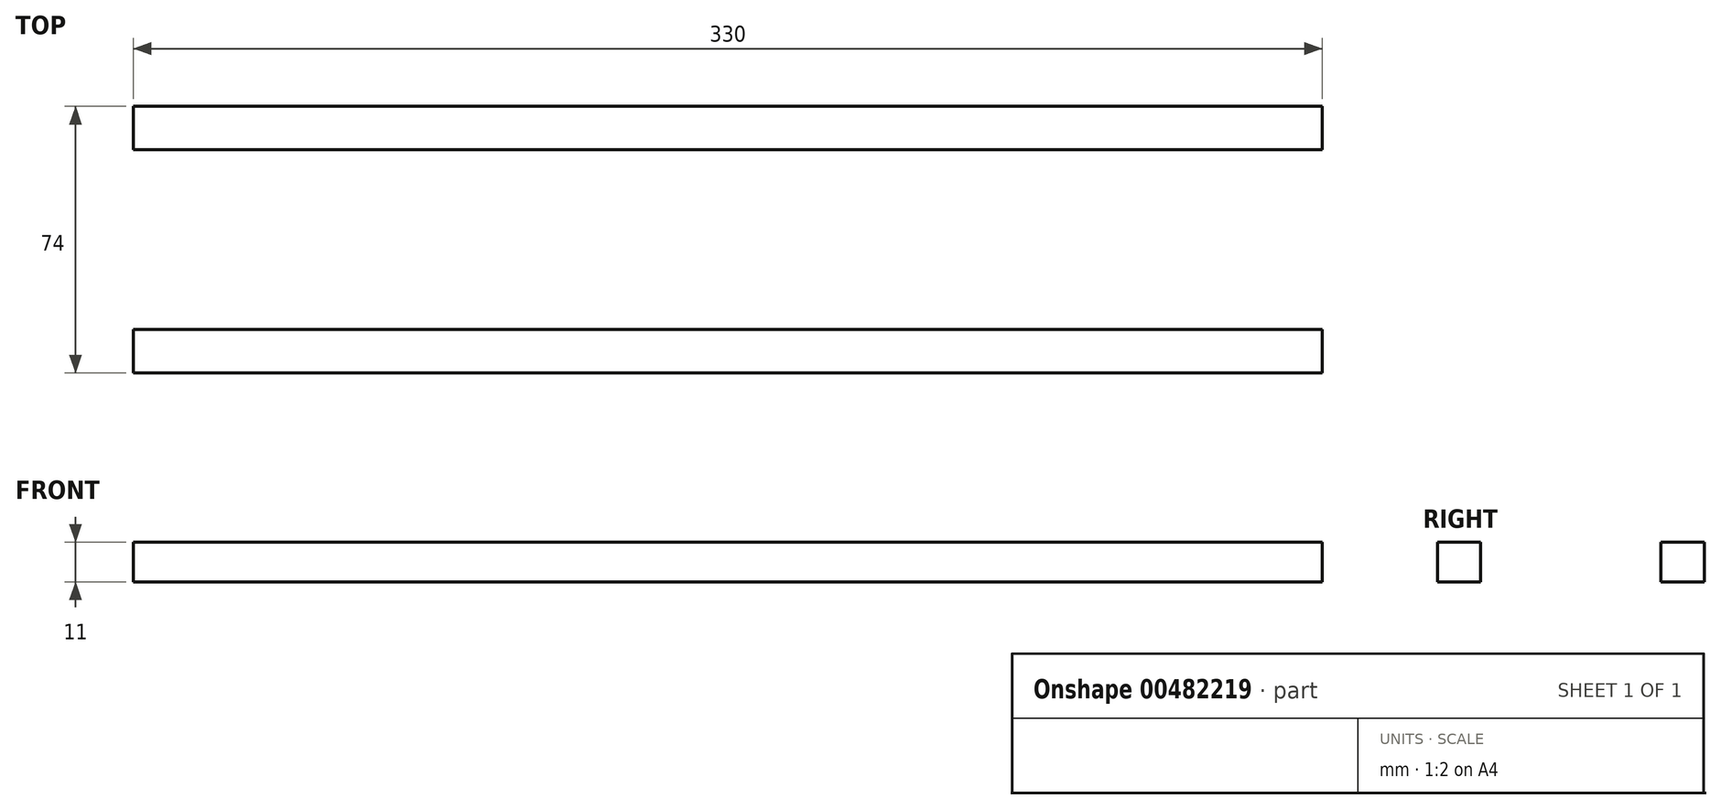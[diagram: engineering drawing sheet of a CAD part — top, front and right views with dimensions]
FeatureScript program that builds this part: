
annotation { "Feature Type Name" : "Feature", "Feature Type Description" : "" }
export const myFeature = defineFeature(function(context is Context, id is Id, definition is map)
    precondition{}
    {
        {
            var Q0;
            Q0=qCreatedBy(makeId("Top.planeOp"),FACE);
            var sketch = newSketch(context, id + "F0", { "sketchPlane" : qUnion([Q0])});
            skLineSegment(sketch, "E0.bottom", {"start": v(0, 0) * mm, "end": v(500, 0) * mm});
            skLineSegment(sketch, "E0.top", {"start": v(0, 350) * mm, "end": v(500, 350) * mm});
            skLineSegment(sketch, "E0.left", {"start": v(0, 0) * mm, "end": v(0, 350) * mm});
            skLineSegment(sketch, "E0.right", {"start": v(500, 0) * mm, "end": v(500, 350) * mm});
            skLineSegment(sketch, "E1.bottom", {"start": v(155, 63) * mm, "end": v(485, 63) * mm});
            skLineSegment(sketch, "E1.top", {"start": v(155, 75) * mm, "end": v(485, 75) * mm});
            skLineSegment(sketch, "E1.left", {"start": v(155, 63) * mm, "end": v(155, 75) * mm});
            skLineSegment(sketch, "E1.right", {"start": v(485, 63) * mm, "end": v(485, 75) * mm});
            skLineSegment(sketch, "E2.bottom", {"start": v(155, 125) * mm, "end": v(485, 125) * mm});
            skLineSegment(sketch, "E2.top", {"start": v(155, 137) * mm, "end": v(485, 137) * mm});
            skLineSegment(sketch, "E2.left", {"start": v(155, 125) * mm, "end": v(155, 137) * mm});
            skLineSegment(sketch, "E2.right", {"start": v(485, 125) * mm, "end": v(485, 137) * mm});
            skLineSegment(sketch, "E3", {"start": v(115, 135) * mm, "end": v(115, 135) * mm});
            skCircle(sketch, "E4", {"center": v(107, 135) * mm, "radius": 3 * mm});
            skCircle(sketch, "E5.MirrorC", {"center": v(123, 135) * mm, "radius": 3 * mm});
            skCircle(sketch, "E6", {"center": v(107, 65) * mm, "radius": 3 * mm});
            skCircle(sketch, "E7.MirrorC", {"center": v(123, 65) * mm, "radius": 3 * mm});
            skPoint(sketch, "E8", {"position": v(320, 42.5) * mm});
            skPoint(sketch, "E9", {"position": v(245, 42.5) * mm});
            skPoint(sketch, "E10", {"position": v(395, 42.5) * mm});
            skCircle(sketch, "E11", {"center": v(170, 42.5) * mm, "radius": 3 * mm});
            skCircle(sketch, "E12", {"center": v(245, 42.5) * mm, "radius": 3 * mm});
            skCircle(sketch, "E13", {"center": v(320, 42.5) * mm, "radius": 3 * mm});
            skCircle(sketch, "E14", {"center": v(395, 42.5) * mm, "radius": 3 * mm});
            skCircle(sketch, "E15", {"center": v(470, 42.5) * mm, "radius": 3 * mm});
            skCircle(sketch, "E16.MirrorC", {"center": v(395, 157.5) * mm, "radius": 3 * mm});
            skCircle(sketch, "E17.MirrorC", {"center": v(245, 157.5) * mm, "radius": 3 * mm});
            skCircle(sketch, "E18.MirrorC", {"center": v(320, 157.5) * mm, "radius": 3 * mm});
            skCircle(sketch, "E19.MirrorC", {"center": v(170, 157.5) * mm, "radius": 3 * mm});
            skCircle(sketch, "E20.MirrorC", {"center": v(470, 157.5) * mm, "radius": 3 * mm});
            skCircle(sketch, "E21", {"center": v(478.61, 256.5) * mm, "radius": 2.5 * mm});
            skCircle(sketch, "E22", {"center": v(478.54, 298.5) * mm, "radius": 2.5 * mm});
            skCircle(sketch, "E23.MirrorC", {"center": v(123.46, 298.5) * mm, "radius": 2.5 * mm});
            skCircle(sketch, "E24.MirrorC", {"center": v(123.39, 256.5) * mm, "radius": 2.5 * mm});
            skLineSegment(sketch, "E25.bottom", {"start": v(91.34, 620.44) * mm, "end": v(104.34, 620.44) * mm});
            skLineSegment(sketch, "E25.top", {"start": v(91.34, 579.44) * mm, "end": v(104.34, 579.44) * mm});
            skLineSegment(sketch, "E25.left", {"start": v(91.34, 620.44) * mm, "end": v(91.34, 579.44) * mm});
            skLineSegment(sketch, "E25.right", {"start": v(104.34, 620.44) * mm, "end": v(104.34, 579.44) * mm});
            skCircle(sketch, "E26", {"center": v(97.96, 583.94) * mm, "radius": 2.5 * mm});
            skCircle(sketch, "E27", {"center": v(97.88, 615.94) * mm, "radius": 2.5 * mm});
            skSolve(sketch);
        }
        {
            var Q0;
            Q0=makeQuery(id+"F0.imprint","IMPRINT",FACE,{"disambiguationData":[TD([[makeQuery(id+"F0.imprint","IMPRINT",EDGE,{"derivedFrom":sQuery(id+"F0.wireOp",EDGE,"E0.bottom")}),1.0]])]});
            var Q1;
            Q1=makeQuery(id+"F0.imprint","IMPRINT",FACE,{"disambiguationData":[TD([[makeQuery(id+"F0.imprint","IMPRINT",EDGE,{"derivedFrom":sQuery(id+"F0.wireOp",EDGE,"uNRts3Xr-A0tI-6eeH-C82y-h4EAb9lMHTzn.bottom")}),-1.0]])]});
            var Q2;
            Q2=makeQuery(id+"F0.imprint","IMPRINT",FACE,{"disambiguationData":[TD([[makeQuery(id+"F0.imprint","IMPRINT",EDGE,{"derivedFrom":sQuery(id+"F0.wireOp",EDGE,"E2.bottom")}),1.0]])]});
            var Q3;
            Q3=makeQuery(id+"F0.imprint","IMPRINT",FACE,{"disambiguationData":[TD([[makeQuery(id+"F0.imprint","IMPRINT",EDGE,{"derivedFrom":sQuery(id+"F0.wireOp",EDGE,"4c47dcb6-4724-46bd-bd65-4ab124e978fb0.MirrorCS")}),1.0]])]});
            var Q4;
            Q4=makeQuery(id+"F0.imprint","IMPRINT",FACE,{"disambiguationData":[TD([[makeQuery(id+"F0.imprint","IMPRINT",EDGE,{"derivedFrom":sQuery(id+"F0.wireOp",EDGE,"a6b73269-a802-4449-93f2-79380c040cbc.bottom")}),-1.0]])]});
            var Q5;
            Q5=makeQuery(id+"F0.imprint","IMPRINT",FACE,{"disambiguationData":[TD([[makeQuery(id+"F0.imprint","IMPRINT",EDGE,{"derivedFrom":sQuery(id+"F0.wireOp",EDGE,"yu3ANbIo-FdIO-HU7t-2UAq-bTAXw5hcEbcA.bottom")}),-1.0]])]});
            var Q6;
            Q6=makeQuery(id+"F0.imprint","IMPRINT",FACE,{"disambiguationData":[TD([[makeQuery(id+"F0.imprint","IMPRINT",EDGE,{"derivedFrom":sQuery(id+"F0.wireOp",EDGE,"E17.MirrorC")}),-1.0]])]});
            var Q7;
            Q7=makeQuery(id+"F0.imprint","IMPRINT",FACE,{"disambiguationData":[TD([[makeQuery(id+"F0.imprint","IMPRINT",EDGE,{"derivedFrom":sQuery(id+"F0.wireOp",EDGE,"E16.MirrorC")}),-1.0]])]});
            var Q8;
            Q8=makeQuery(id+"F0.imprint","IMPRINT",FACE,{"disambiguationData":[TD([[makeQuery(id+"F0.imprint","IMPRINT",EDGE,{"derivedFrom":sQuery(id+"F0.wireOp",EDGE,"E15")}),1.0]])]});
            var Q9;
            Q9=makeQuery(id+"F0.imprint","IMPRINT",FACE,{"disambiguationData":[TD([[makeQuery(id+"F0.imprint","IMPRINT",EDGE,{"derivedFrom":sQuery(id+"F0.wireOp",EDGE,"E14")}),1.0]])]});
            var Q10;
            Q10=makeQuery(id+"F0.imprint","IMPRINT",FACE,{"disambiguationData":[TD([[makeQuery(id+"F0.imprint","IMPRINT",EDGE,{"derivedFrom":sQuery(id+"F0.wireOp",EDGE,"E13")}),1.0]])]});
            var Q11;
            Q11=makeQuery(id+"F0.imprint","IMPRINT",FACE,{"disambiguationData":[TD([[makeQuery(id+"F0.imprint","IMPRINT",EDGE,{"derivedFrom":sQuery(id+"F0.wireOp",EDGE,"E11")}),1.0]])]});
            var Q12;
            Q12=makeQuery(id+"F0.imprint","IMPRINT",FACE,{"disambiguationData":[TD([[makeQuery(id+"F0.imprint","IMPRINT",EDGE,{"derivedFrom":sQuery(id+"F0.wireOp",EDGE,"E12")}),1.0]])]});
            var Q13;
            Q13=makeQuery(id+"F0.imprint","IMPRINT",FACE,{"disambiguationData":[TD([[makeQuery(id+"F0.imprint","IMPRINT",EDGE,{"derivedFrom":sQuery(id+"F0.wireOp",EDGE,"E7.MirrorC")}),-1.0]])]});
            var Q14;
            Q14=makeQuery(id+"F0.imprint","IMPRINT",FACE,{"disambiguationData":[TD([[makeQuery(id+"F0.imprint","IMPRINT",EDGE,{"derivedFrom":sQuery(id+"F0.wireOp",EDGE,"E6")}),1.0]])]});
            var Q15;
            Q15=makeQuery(id+"F0.imprint","IMPRINT",FACE,{"disambiguationData":[TD([[makeQuery(id+"F0.imprint","IMPRINT",EDGE,{"derivedFrom":sQuery(id+"F0.wireOp",EDGE,"E5.MirrorC")}),-1.0]])]});
            var Q16;
            Q16=makeQuery(id+"F0.imprint","IMPRINT",FACE,{"disambiguationData":[TD([[makeQuery(id+"F0.imprint","IMPRINT",EDGE,{"derivedFrom":sQuery(id+"F0.wireOp",EDGE,"E19.MirrorC")}),-1.0]])]});
            var Q17;
            Q17=makeQuery(id+"F0.imprint","IMPRINT",FACE,{"disambiguationData":[TD([[makeQuery(id+"F0.imprint","IMPRINT",EDGE,{"derivedFrom":sQuery(id+"F0.wireOp",EDGE,"E18.MirrorC")}),-1.0]])]});
            var Q18;
            Q18=makeQuery(id+"F0.imprint","IMPRINT",FACE,{"disambiguationData":[TD([[makeQuery(id+"F0.imprint","IMPRINT",EDGE,{"derivedFrom":sQuery(id+"F0.wireOp",EDGE,"E20.MirrorC")}),-1.0]])]});
            var Q19;
            Q19=makeQuery(id+"F0.imprint","IMPRINT",FACE,{"disambiguationData":[TD([[makeQuery(id+"F0.imprint","IMPRINT",EDGE,{"derivedFrom":sQuery(id+"F0.wireOp",EDGE,"E4")}),1.0]])]});
            var Q20;
            Q20=makeQuery(id+"F0.imprint","IMPRINT",FACE,{"disambiguationData":[TD([[makeQuery(id+"F0.imprint","IMPRINT",EDGE,{"derivedFrom":sQuery(id+"F0.wireOp",EDGE,"E22")}),1.0]])]});
            var Q21;
            Q21=makeQuery(id+"F0.imprint","IMPRINT",FACE,{"disambiguationData":[TD([[makeQuery(id+"F0.imprint","IMPRINT",EDGE,{"derivedFrom":sQuery(id+"F0.wireOp",EDGE,"309a9aaa-b51d-4d3a-aa64-c8353506e3b9")}),1.0]])]});
            var Q22;
            Q22=makeQuery(id+"F0.imprint","IMPRINT",FACE,{"disambiguationData":[TD([[makeQuery(id+"F0.imprint","IMPRINT",EDGE,{"derivedFrom":sQuery(id+"F0.wireOp",EDGE,"f062ca2c-7df7-48ee-b907-5a2952540d44")}),1.0]])]});
            var Q23;
            Q23=makeQuery(id+"F0.imprint","IMPRINT",FACE,{"disambiguationData":[TD([[makeQuery(id+"F0.imprint","IMPRINT",EDGE,{"derivedFrom":sQuery(id+"F0.wireOp",EDGE,"E21")}),1.0]])]});
            var Q24;
            Q24=makeQuery(id+"F0.imprint","IMPRINT",FACE,{"disambiguationData":[TD([[makeQuery(id+"F0.imprint","IMPRINT",EDGE,{"derivedFrom":sQuery(id+"F0.wireOp",EDGE,"E23.MirrorC")}),-1.0]])]});
            var Q25;
            Q25=makeQuery(id+"F0.imprint","IMPRINT",FACE,{"disambiguationData":[TD([[makeQuery(id+"F0.imprint","IMPRINT",EDGE,{"derivedFrom":sQuery(id+"F0.wireOp",EDGE,"E24.MirrorC")}),-1.0]])]});
            var Q26;
            Q26=makeQuery(id+"F0.imprint","IMPRINT",FACE,{"disambiguationData":[TD([[makeQuery(id+"F0.imprint","IMPRINT",EDGE,{"derivedFrom":sQuery(id+"F0.wireOp",EDGE,"E1.bottom")}),1.0]])]});
            extrude(context, id + "F1", {"entities" : qUnion([Q0, Q1, Q2, Q3, Q4, Q5, Q6, Q7, Q8, Q9, Q10, Q11, Q12, Q13, Q14, Q15, Q16, Q17, Q18, Q19, Q20, Q21, Q22, Q23, Q24, Q25, Q26]), "oppositeDirection" : true, "depth" : 20 * mm});
        }
        {
            var Q0;
            Q0=makeQuery(id+"F0.imprint","IMPRINT",FACE,{"disambiguationData":[TD([[makeQuery(id+"F0.imprint","IMPRINT",EDGE,{"derivedFrom":sQuery(id+"F0.wireOp",EDGE,"E2.bottom")}),1.0]])]});
            var Q1;
            Q1=makeQuery(id+"F0.imprint","IMPRINT",FACE,{"disambiguationData":[TD([[makeQuery(id+"F0.imprint","IMPRINT",EDGE,{"derivedFrom":sQuery(id+"F0.wireOp",EDGE,"E1.bottom")}),1.0]])]});
            extrude(context, id + "F2", {"entities" : qUnion([Q0, Q1]), "operationType" : NewBodyOperationType.REMOVE, "oppositeDirection" : true, "depth" : 9 * mm});
        }
        {
            var Q0;
            Q0=makeQuery(id+"F0.imprint","IMPRINT",FACE,{"disambiguationData":[TD([[makeQuery(id+"F0.imprint","IMPRINT",EDGE,{"derivedFrom":sQuery(id+"F0.wireOp",EDGE,"E11")}),1.0]])]});
            var Q1;
            Q1=makeQuery(id+"F0.imprint","IMPRINT",FACE,{"disambiguationData":[TD([[makeQuery(id+"F0.imprint","IMPRINT",EDGE,{"derivedFrom":sQuery(id+"F0.wireOp",EDGE,"E12")}),1.0]])]});
            var Q2;
            Q2=makeQuery(id+"F0.imprint","IMPRINT",FACE,{"disambiguationData":[TD([[makeQuery(id+"F0.imprint","IMPRINT",EDGE,{"derivedFrom":sQuery(id+"F0.wireOp",EDGE,"E13")}),1.0]])]});
            var Q3;
            Q3=makeQuery(id+"F0.imprint","IMPRINT",FACE,{"disambiguationData":[TD([[makeQuery(id+"F0.imprint","IMPRINT",EDGE,{"derivedFrom":sQuery(id+"F0.wireOp",EDGE,"E14")}),1.0]])]});
            var Q4;
            Q4=makeQuery(id+"F0.imprint","IMPRINT",FACE,{"disambiguationData":[TD([[makeQuery(id+"F0.imprint","IMPRINT",EDGE,{"derivedFrom":sQuery(id+"F0.wireOp",EDGE,"E15")}),1.0]])]});
            var Q5;
            Q5=makeQuery(id+"F0.imprint","IMPRINT",FACE,{"disambiguationData":[TD([[makeQuery(id+"F0.imprint","IMPRINT",EDGE,{"derivedFrom":sQuery(id+"F0.wireOp",EDGE,"E20.MirrorC")}),-1.0]])]});
            var Q6;
            Q6=makeQuery(id+"F0.imprint","IMPRINT",FACE,{"disambiguationData":[TD([[makeQuery(id+"F0.imprint","IMPRINT",EDGE,{"derivedFrom":sQuery(id+"F0.wireOp",EDGE,"E16.MirrorC")}),-1.0]])]});
            var Q7;
            Q7=makeQuery(id+"F0.imprint","IMPRINT",FACE,{"disambiguationData":[TD([[makeQuery(id+"F0.imprint","IMPRINT",EDGE,{"derivedFrom":sQuery(id+"F0.wireOp",EDGE,"E18.MirrorC")}),-1.0]])]});
            var Q8;
            Q8=makeQuery(id+"F0.imprint","IMPRINT",FACE,{"disambiguationData":[TD([[makeQuery(id+"F0.imprint","IMPRINT",EDGE,{"derivedFrom":sQuery(id+"F0.wireOp",EDGE,"E17.MirrorC")}),-1.0]])]});
            var Q9;
            Q9=makeQuery(id+"F0.imprint","IMPRINT",FACE,{"disambiguationData":[TD([[makeQuery(id+"F0.imprint","IMPRINT",EDGE,{"derivedFrom":sQuery(id+"F0.wireOp",EDGE,"E19.MirrorC")}),-1.0]])]});
            var Q10;
            Q10=makeQuery(id+"F0.imprint","IMPRINT",FACE,{"disambiguationData":[TD([[makeQuery(id+"F0.imprint","IMPRINT",EDGE,{"derivedFrom":sQuery(id+"F0.wireOp",EDGE,"E4")}),1.0]])]});
            var Q11;
            Q11=makeQuery(id+"F0.imprint","IMPRINT",FACE,{"disambiguationData":[TD([[makeQuery(id+"F0.imprint","IMPRINT",EDGE,{"derivedFrom":sQuery(id+"F0.wireOp",EDGE,"E5.MirrorC")}),-1.0]])]});
            var Q12;
            Q12=makeQuery(id+"F0.imprint","IMPRINT",FACE,{"disambiguationData":[TD([[makeQuery(id+"F0.imprint","IMPRINT",EDGE,{"derivedFrom":sQuery(id+"F0.wireOp",EDGE,"E7.MirrorC")}),-1.0]])]});
            var Q13;
            Q13=makeQuery(id+"F0.imprint","IMPRINT",FACE,{"disambiguationData":[TD([[makeQuery(id+"F0.imprint","IMPRINT",EDGE,{"derivedFrom":sQuery(id+"F0.wireOp",EDGE,"E6")}),1.0]])]});
            var Q14;
            Q14=makeQuery(id+"F0.imprint","IMPRINT",FACE,{"disambiguationData":[TD([[makeQuery(id+"F0.imprint","IMPRINT",EDGE,{"derivedFrom":sQuery(id+"F0.wireOp",EDGE,"E22")}),1.0]])]});
            var Q15;
            Q15=makeQuery(id+"F0.imprint","IMPRINT",FACE,{"disambiguationData":[TD([[makeQuery(id+"F0.imprint","IMPRINT",EDGE,{"derivedFrom":sQuery(id+"F0.wireOp",EDGE,"E21")}),1.0]])]});
            var Q16;
            Q16=makeQuery(id+"F0.imprint","IMPRINT",FACE,{"disambiguationData":[TD([[makeQuery(id+"F0.imprint","IMPRINT",EDGE,{"derivedFrom":sQuery(id+"F0.wireOp",EDGE,"E24.MirrorC")}),-1.0]])]});
            var Q17;
            Q17=makeQuery(id+"F0.imprint","IMPRINT",FACE,{"disambiguationData":[TD([[makeQuery(id+"F0.imprint","IMPRINT",EDGE,{"derivedFrom":sQuery(id+"F0.wireOp",EDGE,"E23.MirrorC")}),-1.0]])]});
            extrude(context, id + "F3", {"entities" : qUnion([Q0, Q1, Q2, Q3, Q4, Q5, Q6, Q7, Q8, Q9, Q10, Q11, Q12, Q13, Q14, Q15, Q16, Q17]), "operationType" : NewBodyOperationType.REMOVE, "oppositeDirection" : true, "depth" : 20 * mm});
        }
    });
